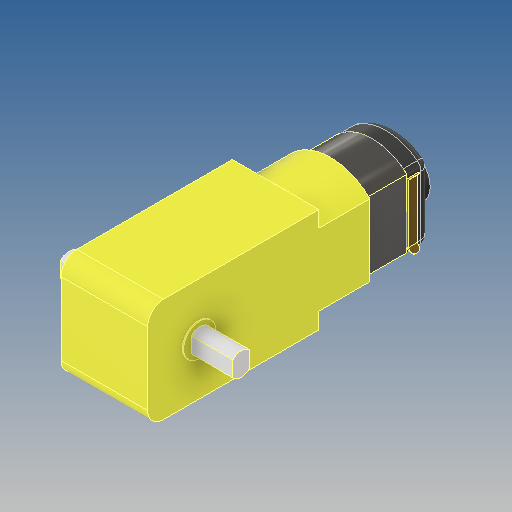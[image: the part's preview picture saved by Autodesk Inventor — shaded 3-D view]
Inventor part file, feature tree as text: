
AUTODESK INVENTOR PART (.ipt)
format: ipt  version: 2020 (Build 240168000, 168)  size: 290,816 bytes
history: native  units: in
note: dims shown in document units (in); Inventor stores cm internally (conversion verified against a paired STEP export)
features: extrude x11, sketch x11, projected_geometry x5, fillet x3, mirror x1
ambient origin geometry x8: Origin, YZ Plane, XZ Plane, XY Plane, X Axis, Y Axis, Z Axis, Center Point
bodies: Solid1 (feature_tree), Solid2 (feature_tree), Solid3 (feature_tree), Solid4 (feature_tree)
feature tree (31):
  extrude  "Extrusion1"  Depth=0.8858in
  fillet  "Fillet1"  Radius=1.4567in
  extrude  "Extrusion2"  Depth=0.1378in
  extrude  "Extrusion3"  Depth=0.6693in
  extrude  "Extrusion4"  Depth=0.0394in
  extrude  "Extrusion5"  Depth=0.1969in TaperAngle=0.0deg
  extrude  "Extrusion6"  Depth=0.4331in
  extrude  "Extrusion7"  Depth=0.1969in
  mirror  "Mirror1"
  extrude  "Extrusion8"  Depth=0.1457in
  fillet  "Fillet2"  Radius=0.0728in
  extrude  "Extrusion9"  Depth=0.3543in
  extrude  "Extrusion10"  Depth=0.0591in TaperAngle=0.0deg
  extrude  "Extrusion11"  Depth=0.3937in
  fillet  "Fillet3"  Radius=0.1673in
  sketch  "Sketch1"  dims[d0=0.7362in d1=0.8858in d2=1.4567in d3=0.0in]
  sketch  "Sketch2"  dims[d4=0.1339in d5=0.1378in]
  sketch  "Sketch3"  dims[d6=0.1378in d7=0.6693in]
  projected_geometry  "Projected Loop1"
  sketch  "Sketch4"  dims[d8=0.4331in d9=0.0in d10=0.0394in]
  projected_geometry  "Projected Loop2"
  sketch  "Sketch5"  dims[d11=0.3543in d12=0.0in d13=0.1969in d14=0.0in]
  sketch  "Sketch6"  dims[d15=0.4331in d16=0.2756in]
  projected_geometry  "Projected Loop3"
  sketch  "Sketch7"  dims[d17=0.0098in d18=0.0in d19=0.1969in]
  projected_geometry  "Projected Loop4"
  sketch  "Sketch8"  dims[d20=0.3543in d21=0.0in d22=0.1457in d23=0.0728in]
  sketch  "Sketch9"  dims[d25=0.3543in d26=0.0in d27=0.1575in]
  projected_geometry  "Projected Loop5"
  sketch  "Sketch10"  dims[d28=0.8661in d29=0.0591in d30=0.0in]
  sketch  "Sketch11"  dims[d31=0.0787in d32=0.3937in d33=0.1673in d34=0.0984in d35=0.0in d36=0.0787in d37=0.0394in d38=0.0in d39=0.0098in d40=0.5906in d41=0.0098in d42=0.0394in d43=0.0787in d44=0.0in d45=0.0394in]
